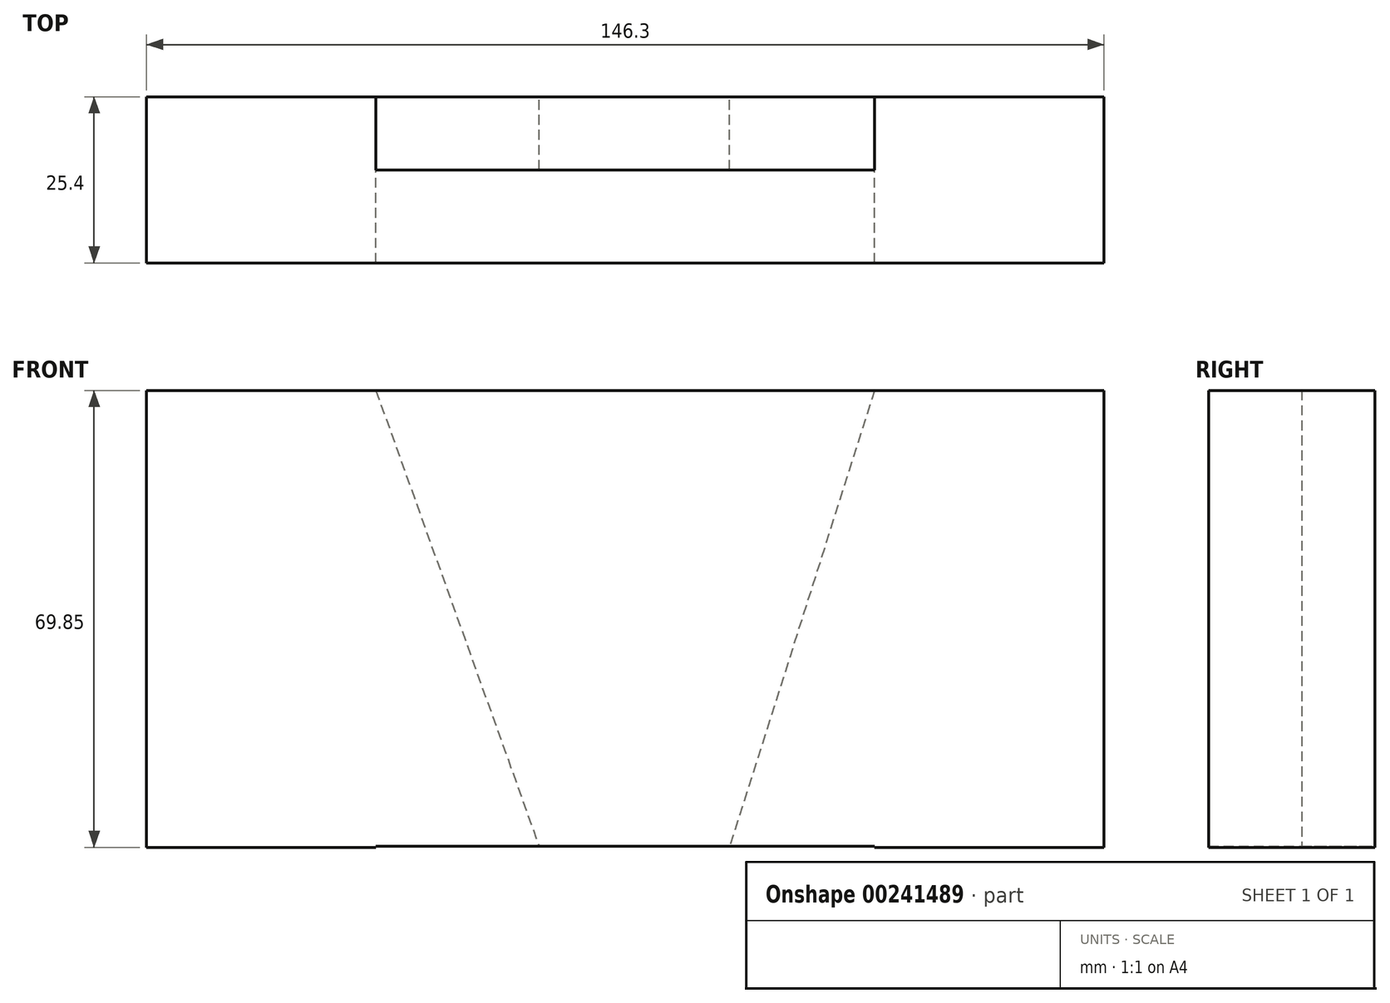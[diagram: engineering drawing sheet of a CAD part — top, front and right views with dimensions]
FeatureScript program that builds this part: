
annotation { "Feature Type Name" : "Feature", "Feature Type Description" : "" }
export const myFeature = defineFeature(function(context is Context, id is Id, definition is map)
    precondition{}
    {
        {
            var Q0;
            Q0=qCreatedBy(makeId("Front.planeOp"),FACE);
            var sketch = newSketch(context, id + "F0", { "sketchPlane" : qUnion([Q0])});
            skLineSegment(sketch, "E0.bottom", {"start": v(-45.26, 38.03) * mm, "end": v(-10.2, 38.03) * mm});
            skLineSegment(sketch, "E0.top", {"start": v(-45.26, -31.82) * mm, "end": v(-10.2, -31.82) * mm});
            skLineSegment(sketch, "E0.left", {"start": v(-45.26, 38.03) * mm, "end": v(-45.26, -31.82) * mm});
            skLineSegment(sketch, "E0.right", {"start": v(-10.2, -31.63) * mm, "end": v(-10.2, -31.82) * mm});
            skLineSegment(sketch, "E1.bottom", {"start": v(-10.2, 38.03) * mm, "end": v(66, 38.03) * mm});
            skLineSegment(sketch, "E1.top", {"start": v(-10.2, -31.63) * mm, "end": v(66, -31.63) * mm});
            skLineSegment(sketch, "E2.bottom", {"start": v(66, 38.03) * mm, "end": v(101.04, 38.03) * mm});
            skLineSegment(sketch, "E2.top", {"start": v(66, -31.82) * mm, "end": v(101.04, -31.82) * mm});
            skLineSegment(sketch, "E2.left", {"start": v(66, -31.63) * mm, "end": v(66, -31.82) * mm});
            skLineSegment(sketch, "E2.right", {"start": v(101.04, 38.03) * mm, "end": v(101.04, -31.82) * mm});
            skLineSegment(sketch, "E3", {"start": v(-10.2, 38.03) * mm, "end": v(14.71, -31.63) * mm});
            skLineSegment(sketch, "E4", {"start": v(66, 38.03) * mm, "end": v(43.84, -31.63) * mm});
            skLineSegment(sketch, "E5", {"start": v(14.71, -31.63) * mm, "end": v(43.84, -31.63) * mm});
            skSolve(sketch);
        }
        {
            var Q0;
            Q0=makeQuery(id+"F0.imprint","IMPRINT",FACE,{"disambiguationData":[TD([[makeQuery(id+"F0.imprint","IMPRINT",EDGE,{"derivedFrom":sQuery(id+"F0.wireOp",EDGE,"E0.bottom")}),-1.0]])]});
            var Q1;
            Q1=makeQuery(id+"F0.imprint","IMPRINT",FACE,{"disambiguationData":[TD([[makeQuery(id+"F0.imprint","IMPRINT",EDGE,{"derivedFrom":sQuery(id+"F0.wireOp",EDGE,"E2.bottom")}),-1.0]])]});
            extrude(context, id + "F1", {"entities" : qUnion([Q0, Q1]), "depth" : 25.4 * mm});
        }
        {
            var Q0;
            Q0=makeQuery(id+"F0.imprint","IMPRINT",FACE,{"disambiguationData":[TD([[makeQuery(id+"F0.imprint","IMPRINT",EDGE,{"derivedFrom":sQuery(id+"F0.wireOp",EDGE,"E1.bottom")}),-1.0]])]});
            extrude(context, id + "F2", {"entities" : qUnion([Q0]), "operationType" : NewBodyOperationType.ADD, "depth" : 25.4 * mm});
        }
        {
            var Q0;
            Q0=makeQuery(id+"F0.imprint","IMPRINT",FACE,{"disambiguationData":[TD([[makeQuery(id+"F0.imprint","IMPRINT",EDGE,{"derivedFrom":sQuery(id+"F0.wireOp",EDGE,"E3")}),1.0]])]});
            extrude(context, id + "F3", {"entities" : qUnion([Q0]), "depth" : 11.18 * mm});
        }
    });
